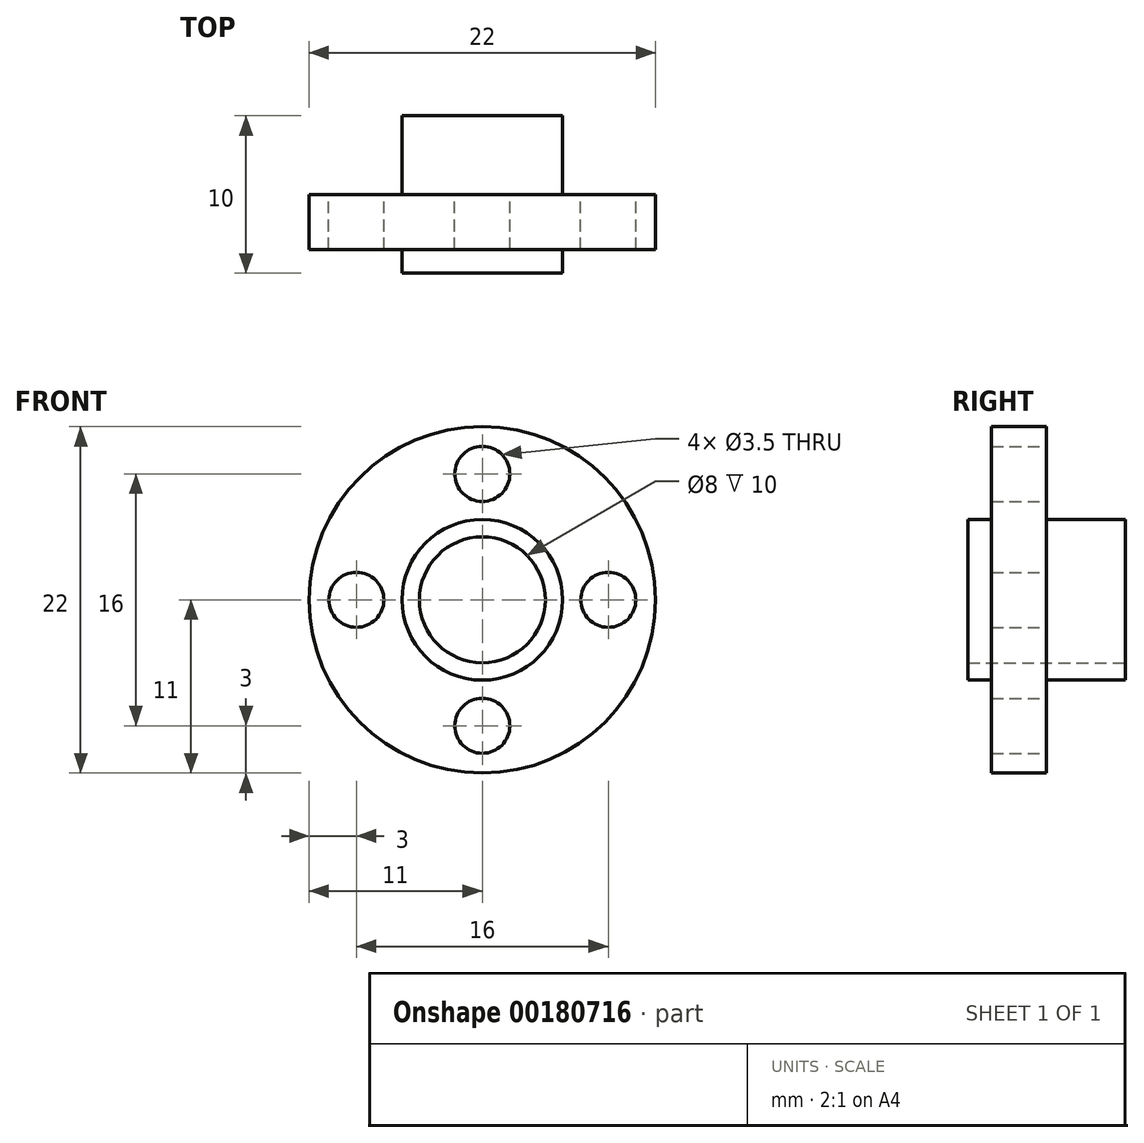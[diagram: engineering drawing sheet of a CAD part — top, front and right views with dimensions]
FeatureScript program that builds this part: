
annotation { "Feature Type Name" : "Feature", "Feature Type Description" : "" }
export const myFeature = defineFeature(function(context is Context, id is Id, definition is map)
    precondition{}
    {
        {
            var Q0;
            Q0=qCreatedBy(makeId("Front.planeOp"),FACE);
            var sketch = newSketch(context, id + "F0", { "sketchPlane" : qUnion([Q0])});
            skCircle(sketch, "E0", {"center": v(0, 0) * mm, "radius": 11 * mm});
            skCircle(sketch, "E1", {"center": v(0, 0) * mm, "radius": 5.1 * mm});
            skCircle(sketch, "E2", {"center": v(0, 0) * mm, "radius": 8 * mm, "construction": true});
            skCircle(sketch, "E3", {"center": v(0, 8) * mm, "radius": 1.75 * mm});
            skCircle(sketch, "E4", {"center": v(0, 0) * mm, "radius": 4 * mm});
            skCircle(sketch, "E5.1.0", {"center": v(-8, 0) * mm, "radius": 1.75 * mm});
            skCircle(sketch, "E5.2.0", {"center": v(0, -8) * mm, "radius": 1.75 * mm});
            skCircle(sketch, "E5.3.0", {"center": v(8, 0) * mm, "radius": 1.75 * mm});
            skSolve(sketch);
        }
        {
            var Q0;
            Q0=makeQuery(id+"F0.imprint","IMPRINT",FACE,{"disambiguationData":[TD([[makeQuery(id+"F0.imprint","IMPRINT",EDGE,{"derivedFrom":sQuery(id+"F0.wireOp",EDGE,"E0")}),1.0]])]});
            extrude(context, id + "F1", {"entities" : qUnion([Q0]), "depth" : 3.5 * mm});
        }
        {
            var Q0;
            Q0=makeQuery(id+"F0.imprint","IMPRINT",FACE,{"disambiguationData":[TD([[makeQuery(id+"F0.imprint","IMPRINT",EDGE,{"derivedFrom":sQuery(id+"F0.wireOp",EDGE,"E1")}),1.0]])]});
            extrude(context, id + "F2", {"entities" : qUnion([Q0]), "operationType" : NewBodyOperationType.ADD, "depth" : 5 * mm});
        }
        {
            var Q0;
            Q0=makeQuery(id+"F2.opExtrude","CAP_FACE",FACE,{"disambiguationData":[OSD([sQuery(id+"F0.wireOp",EDGE,"E1"),sQuery(id+"F0.wireOp",EDGE,"E4")])],"isStart":false});
            extrude(context, id + "F3", {"entities" : qUnion([Q0]), "operationType" : NewBodyOperationType.ADD, "oppositeDirection" : true, "depth" : 10 * mm});
        }
    });
